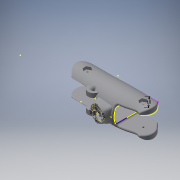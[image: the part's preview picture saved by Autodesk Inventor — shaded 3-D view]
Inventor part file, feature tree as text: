
AUTODESK INVENTOR PART (.ipt)
format: ipt  version: 2016 (Build 200138000, 138)  size: 3,208,704 bytes
history: native  units: mm
features: sketch x54, plane x31, extrude x23, fillet x21, other x9, chamfer x4, hole x3, loft x2
ambient origin geometry x8: Origin, YZ Plane, XZ Plane, XY Plane, X Axis, Y Axis, Z Axis, Center Point
bodies: Solid1 (feature_tree)
feature tree (147):
  sketch  "Sketch1"  dims[d1=8.0mm d2=7.0mm]
  plane  "Work Plane4"
  sketch  "Sketch2"  dims[d3=7.0mm d4=8.0mm d8=20.0mm d9=-3.490659mm d11=8.0mm d12=8.0mm d14=2.0mm d15=10.0mm d17=-1.745329mm d18=1.0mm d19=11.75mm]
  sketch  "Sketch3"  dims[d20=20.0mm d21=9.5mm]
  sketch  "Sketch4"  dims[d22=8.0mm d23=0.0mm d25=9.0mm]
  sketch  "Sketch5"  dims[d27=8.5mm d28=3.0mm]
  sketch  "Sketch6"  dims[d29=-1.745329mm d30=-3.490659mm d31=1.0mm d32=2.0mm d33=8.6mm]
  plane  "Work Plane5"
  sketch  "Sketch7"  dims[d34=8.5mm d35=7.0mm]
  plane  "Work Plane7"
  sketch  "Sketch8"  dims[d36=7.0mm d37=5.0mm d38=3.0mm]
  plane  "Work Plane8"
  sketch  "Sketch9"  dims[d39=17.0mm]
  plane  "Work Plane10"
  sketch  "Sketch10"  dims[d40=8.0mm]
  plane  "Work Plane11"
  plane  "Work Plane12"
  sketch  "Sketch11"  dims[d41=17.0mm]
  sketch  "Sketch12"  dims[d42=7.7mm]
  sketch  "Sketch13"  dims[d43=17.0mm]
  plane  "Work Plane13"
  plane  "Work Plane14"
  plane  "Work Plane15"
  plane  "Work Plane16"
  sketch  "Sketch14"  dims[d44=6.8mm]
  sketch  "Sketch15"  dims[d45=17.0mm]
  plane  "Work Plane20"
  sketch  "Sketch16"  dims[d46=5.0mm]
  sketch  "Sketch17"  dims[d47=2.0mm]
  sketch  "Sketch18"  dims[d48=17.0mm]
  sketch  "Sketch19"  dims[d49=2.0mm]
  plane  "Work Plane21"
  loft  "Loft1"
  extrude  "Extrusion1"  Depth=1.0mm
  fillet  "Fillet1"  [1 undecoded]
  fillet  "Fillet2"  Radius=8.0mm
  fillet  "Fillet3"  Radius=2.0mm
  fillet  "Fillet4"  Radius=10.0mm
  fillet  "Fillet5"  Radius=1.0mm
  fillet  "Fillet6"  Radius=11.75mm
  plane  "Work Plane23"
  plane  "Work Plane25"
  sketch  "Sketch22"  dims[d61=0.0mm d62=90.0deg d63=0.0mm d64=90.0deg]
  plane  "Work Plane27"
  sketch  "Sketch26"  dims[d65=0.0mm d66=90.0deg d67=0.0mm d68=90.0deg d69=0.0mm d70=90.0deg]
  extrude  "Extrusion4"  Depth=9.5mm
  plane  "Work Plane28"
  plane  "Work Plane29"
  extrude  "Extrusion5"  Depth=9.0mm
  extrude  "Extrusion6"  Depth=3.0mm
  fillet  "Fillet7"  Radius=8.6mm
  extrude  "Extrusion7"  Depth=7.0mm
  extrude  "Extrusion9"  Depth=5.0mm
  sketch  "Sketch32"  dims[d91=45.0deg d92=15.0mm d93=0.0mm]
  chamfer  "Chamfer1"  Angle=90.0deg  [1 undecoded]
  sketch  "Sketch33"  dims[d94=2.0mm]
  sketch  "Sketch34"  dims[d95=2.0mm]
  extrude  "Extrusion10"  TaperAngle=0.0deg  [1 undecoded]
  fillet  "Fillet8"  [1 undecoded]
  fillet  "Fillet10"  [1 undecoded]
  extrude  "Extrusion11"  TaperAngle=0.0deg  [1 undecoded]
  extrude  "Extrusion12"  TaperAngle=0.0deg  [1 undecoded]
  fillet  "Fillet11"  [1 undecoded]
  extrude  "Extrusion13"  TaperAngle=0.0deg  [1 undecoded]
  extrude  "Extrusion14"  TaperAngle=0.0deg  [1 undecoded]
  extrude  "Extrusion15"  TaperAngle=0.0deg  [1 undecoded]
  extrude  "Extrusion16"  Depth=2.0mm
  fillet  "Fillet12"  Radius=6.0mm
  fillet  "Fillet13"  Radius=6.0mm
  fillet  "Fillet14"  Radius=2.0mm
  fillet  "Fillet15"  [1 undecoded]
  chamfer  "Chamfer2"  Distance=15.0mm
  chamfer  "Chamfer3"  Distance=22.0mm Angle=90.0deg
  extrude  "Extrusion17"  Depth=3.0mm
  extrude  "Extrusion18"  Depth=12.0mm
  extrude  "Extrusion19"  Depth=15.0mm
  fillet  "Fillet16"  Radius=29.0mm
  sketch  "Sketch44"  dims[d140=1.2mm d141=8.0mm d142=8.0mm d143=2.1mm d144=29.0mm d145=10.75mm d146=200.0mm d147=0.0mm]
  extrude  "Extrusion21"  Depth=12.0mm
  extrude  "Extrusion23"  Depth=200.0mm TaperAngle=0.0deg
  extrude  "Extrusion25"  Depth=12.0mm
  extrude  "Extrusion26"  Depth=12.2mm
  chamfer  "Chamfer4"  Distance=22.0mm
  extrude  "Extrusion27"  Depth=1.0mm TaperAngle=0.0deg
  fillet  "Fillet17"  Radius=29.0mm
  extrude  "Extrusion28"  Depth=40.0mm
  other  "Work Point2"
  plane  "Work Plane30"
  sketch  "Sketch54"  dims[d178=7.0mm d179=1.2mm]
  sketch  "Sketch55"  dims[d180=2.0mm d181=2.0mm d182=45.0deg d183=10.0mm]
  sketch  "Sketch56"  dims[d184=10.0mm d185=11.0mm d186=1.0mm]
  plane  "Work Plane31"
  sketch  "Sketch57"  dims[d187=11.0mm]
  plane  "Work Plane32"
  other  "Work Point5"
  other  "Work Point6"
  other  "Work Point7"
  other  "Work Axis2"
  other  "Work Point8"
  sketch  "Sketch58"  dims[d188=1.0mm]
  other  "Work Point9"
  loft  "Loft2"
  fillet  "Fillet18"  Radius=9.3mm
  fillet  "Fillet19"  Radius=9.3mm
  fillet  "Fillet20"  [1 undecoded]
  fillet  "Fillet21"  Radius=40.0mm
  extrude  "Extrusion30"  Depth=11.5mm
  sketch  "Sketch62"  dims[d193=0.8mm d194=23.0mm d195=0.2mm d196=19.5mm d197=6.0mm d198=12.0mm d199=25.0mm d200=0.0mm d201=1.0mm d202=1.0mm d203=135.0deg d204=14.5mm d205=12.0mm d206=40.0mm d207=0.0mm d208=0.8mm d209=5.0mm d210=5.0mm d211=2.3mm d212=8.5mm d213=1.0mm d214=40.0mm d215=0.0mm d216=3.1mm d217=6.2mm d218=3.0mm d219=0.0mm d220=3.0mm d221=0.0mm d222=12.0mm d223=5.0mm d224=3.0mm d225=0.0mm d226=0.8mm d227=0.2mm d228=0.2mm d229=0.2mm d230=2.0mm d231=2.0mm d232=45.0deg d233=1.0mm d234=2.0mm d235=45.0deg d236=10.75mm d237=11.0mm d238=40.0mm d239=10.0mm d240=7.0mm d241=4.5mm d242=4.5mm d243=4.0mm d244=4.0mm d245=0.0mm d246=8.0mm d247=4.0mm d248=0.0mm d249=8.0mm d250=4.0mm d251=0.0mm d252=1.5mm d253=0.6mm d259=11.0mm d260=10.75mm d261=100.0mm d262=0.0mm d267=2.7mm d268=1.9mm d269=4.3mm d270=11.5mm d271=11.5mm d272=30.0mm d273=0.0mm d277=8.0mm d278=1.0mm d279=0.0mm d280=8.0mm d281=1.0mm d282=0.0mm d283=1.0mm d284=2.0mm d285=45.0deg d286=4.1mm d287=8.2mm d288=10.0mm d289=2.0mm d290=0.0mm d291=0.0mm d292=2.0mm d293=4.5mm d294=3.0mm d295=1.5mm d296=0.0mm d297=0.0mm d302=-1.9mm d303=6.5mm d304=5.75mm d305=11.0mm d306=0.0mm d307=90.0deg d308=0.0mm d309=90.0deg d311=2.0mm d312=2.0mm d313=2.0mm d314=2.0mm d315=2.0mm d316=2.0mm d317=2.0mm d318=0.2mm d319=0.1mm d320=0.05mm d321=3.5mm d322=3.5mm d323=4.5mm d324=0.0mm d325=0.5mm d326=0.5mm d327=2.0mm d328=6.0mm d329=4.0mm d330=2.0mm d331=90.0deg d332=2.0mm d333=0.0mm d334=1.0mm d335=1.0mm d336=1.0mm d337=6.0mm d338=4.0mm d339=2.0mm d340=90.0deg d341=4.5mm d342=0.0mm d343=3.0mm d344=6.0mm d345=6.0mm d346=2.0mm d347=90.0deg d348=4.0mm d349=0.0mm d350=1.0mm]
  hole  "Hole1"  [1 undecoded]
  hole  "Hole2"  [1 undecoded]
  hole  "Hole3"  [1 undecoded]
  fillet  "Fillet22"  Radius=1.0mm
  plane  "Work Plane1"
  plane  "Work Plane2"
  plane  "Work Plane3"
  plane  "Work Plane6"
  plane  "Work Plane9"
  plane  "Work Plane17"
  plane  "Work Plane18"
  plane  "Work Plane19"
  sketch  "Sketch20"  dims[d50=2.0mm d51=0.0mm d52=90.0deg]
  sketch  "Sketch21"  dims[d53=0.0mm d54=90.0deg d55=0.0mm d56=90.0deg d57=0.0mm d58=90.0deg d59=0.0mm d60=90.0deg]
  plane  "Work Plane22"
  plane  "Work Plane24"
  sketch  "Sketch27"  dims[d71=0.0mm d72=90.0deg d73=0.0mm d74=90.0deg]
  sketch  "Sketch28"  dims[d75=0.0mm d76=90.0deg d77=0.0mm d78=90.0deg]
  sketch  "Sketch29"  dims[d79=0.0mm d80=90.0deg d81=0.0mm d82=90.0deg]
  sketch  "Sketch30"  dims[d83=0.0mm d84=90.0deg d85=0.3mm d86=6.0mm d87=6.0mm d88=2.0mm d89=135.0deg]
  sketch  "Sketch31"  dims[d90=2.0mm]
  sketch  "Sketch36"  dims[d96=2.0mm]
  sketch  "Sketch37"  dims[d97=2.0mm]
  sketch  "Sketch38"  dims[d98=2.0mm]
  sketch  "Sketch39"  dims[d99=2.0mm d100=90.0deg d101=22.0mm]
  sketch  "Sketch40"  dims[d102=12.217305mm d103=20.0mm d110=3.0mm]
  sketch  "Sketch41"  dims[d111=6.0mm d112=12.0mm]
  sketch  "Sketch42"  dims[d113=6.0mm d124=15.0mm d135=29.0mm]
  sketch  "Sketch43"  dims[d136=200.0mm d137=0.0mm d138=-25.0mm d139=12.0mm]
  sketch  "Sketch46"  dims[d148=30.0mm d149=12.0mm]
  sketch  "Sketch48"  dims[d150=6.1mm d151=12.2mm d152=22.0mm d153=0.0mm]
  sketch  "Sketch50"  dims[d154=1.0mm d155=20.3mm d156=0.0mm d157=29.0mm]
  sketch  "Sketch51"  dims[d158=10.75mm d159=40.0mm]
  sketch  "Sketch52"  dims[d160=9.3mm d161=1.2mm d162=9.3mm d163=9.3mm d164=180.0deg d167=40.0mm d168=0.0mm]
  sketch  "Sketch53"  dims[d169=29.0mm d170=10.75mm d171=40.0mm d172=9.3mm d173=2.3mm d174=9.3mm d175=9.3mm d176=180.0deg d177=11.5mm]
  other  "Work Point3"
  other  "Work Point4"
  sketch  "Sketch59"  dims[d189=40.0mm d190=0.0mm]
  sketch  "Sketch61"  dims[d191=0.4mm]
note: 16 required parameter values undecoded (feature->parameter linkage not recoverable at this tier; creation-order binding heuristic only, values carry confidence <= 0.55)
